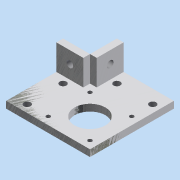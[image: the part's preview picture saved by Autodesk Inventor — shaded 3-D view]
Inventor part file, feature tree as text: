
AUTODESK INVENTOR PART (.ipt)
format: ipt  version: 2015 (Build 190159000, 159)  size: 156,160 bytes
history: native  units: mm
features: sketch x4, hole x4, extrude x2
ambient origin geometry x8: Origin, YZ Plane, XZ Plane, XY Plane, X Axis, Y Axis, Z Axis, Center Point
bodies: Solid1 (feature_tree)
feature tree (10):
  sketch  "Sketch1"  dims[d0=42.3mm d1=23.0mm]
  extrude  "Extrusion1"  Depth=42.3mm
  hole  "Hole1"  [1 undecoded]
  hole  "Hole2"  [1 undecoded]
  extrude  "Extrusion2"  Depth=42.3mm
  hole  "Hole3"  [1 undecoded]
  hole  "Hole4"  [1 undecoded]
  sketch  "Sketch3"  dims[d2=31.0mm d3=31.0mm]
  sketch  "Sketch4"  dims[d4=31.0mm d8=31.0mm]
  sketch  "Sketch5"  dims[d12=21.15mm d16=42.3mm d17=5.65mm d18=5.65mm d19=5.65mm d20=5.65mm d21=20.0mm d22=20.0mm d23=5.0mm d24=0.0mm d25=3.0mm d26=6.0mm d27=4.0mm d28=2.0mm d29=90.0deg d30=8.0mm d31=20.594885mm d32=5.0mm d33=6.0mm d34=4.0mm d35=2.0mm d36=90.0deg d37=8.0mm d38=20.594885mm d39=21.15mm d40=5.0mm d41=5.0mm d42=10.0mm d43=10.0mm d44=19.0mm d45=0.0mm d46=10.0mm d47=10.0mm d50=5.0mm d51=6.0mm d52=4.0mm d53=2.0mm d54=90.0deg d55=8.0mm d56=20.594885mm d58=10.0mm d59=10.0mm d61=5.0mm d62=6.0mm d63=4.0mm d64=2.0mm d65=90.0deg d66=8.0mm d67=20.594885mm]
note: 4 required parameter values undecoded (feature->parameter linkage not recoverable at this tier; creation-order binding heuristic only, values carry confidence <= 0.55)
